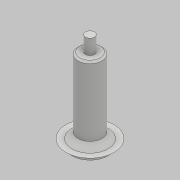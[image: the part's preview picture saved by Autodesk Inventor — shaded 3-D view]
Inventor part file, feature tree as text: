
AUTODESK INVENTOR PART (.ipt)
format: ipt  version: 2018 (Build 220112000, 112)  size: 103,424 bytes
history: native  units: mm
features: other x2, chamfer x1, sketch x1
ambient origin geometry x8: Origin, YZ Plane, XZ Plane, XY Plane, X Axis, Y Axis, Z Axis, Center Point
bodies: Body1 (feature_tree)
feature tree (4):
  other  "實體1"
  other  "迴轉1"
  chamfer  "倒角1"  Distance=7.5mm
  sketch  "草圖1"
